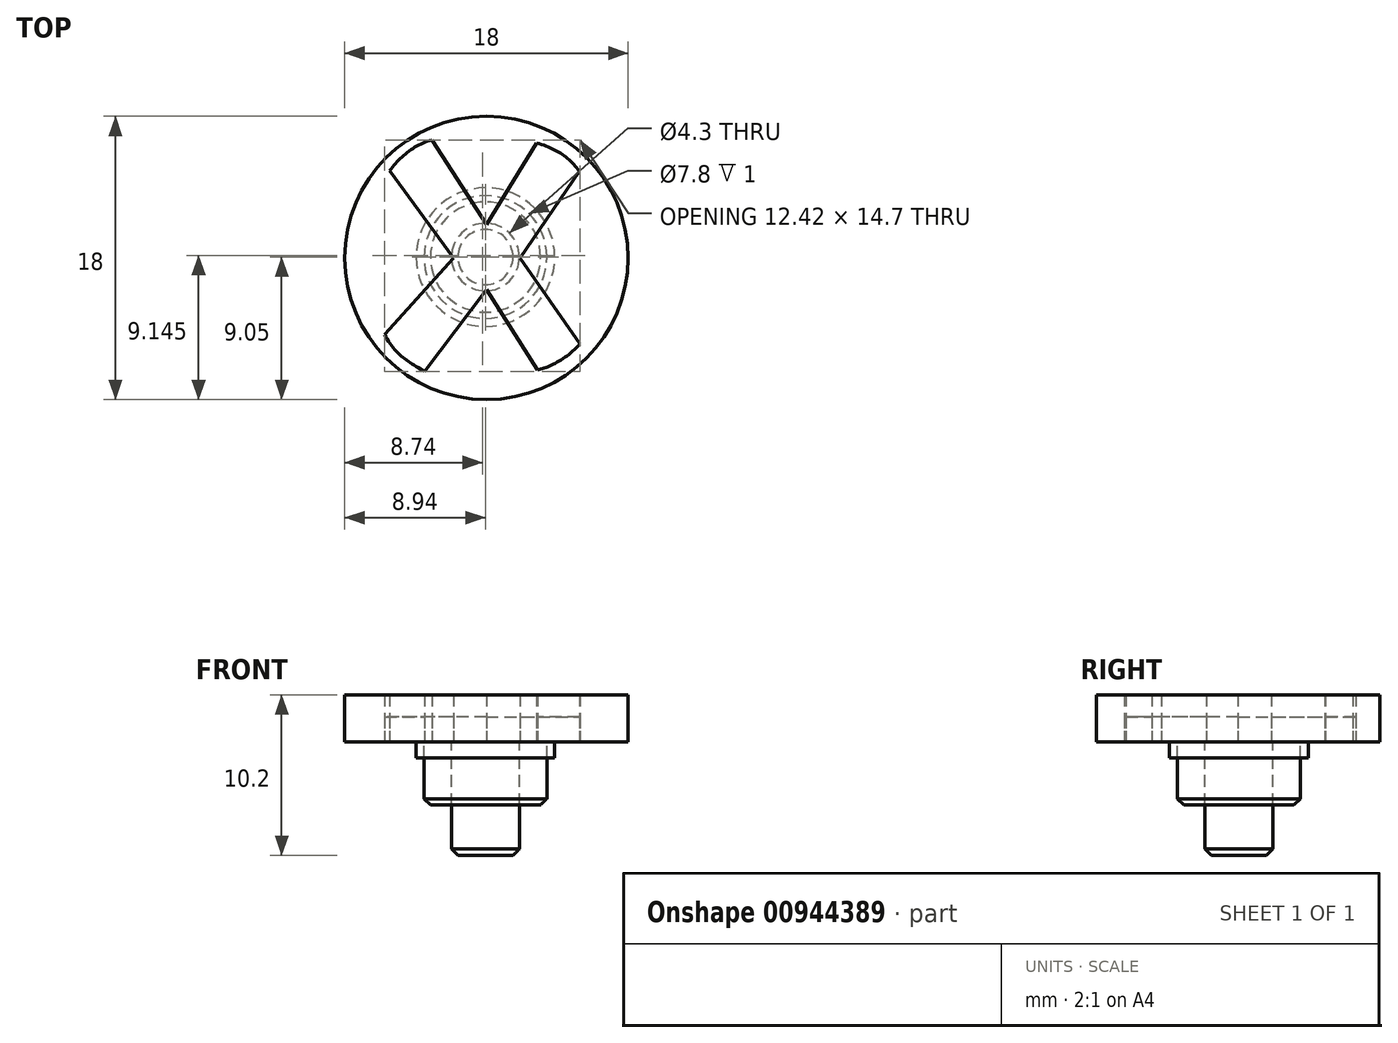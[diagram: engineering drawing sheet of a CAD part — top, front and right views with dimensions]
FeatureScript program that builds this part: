
annotation { "Feature Type Name" : "Feature", "Feature Type Description" : "" }
export const myFeature = defineFeature(function(context is Context, id is Id, definition is map)
    precondition{}
    {
        {
            var Q0;
            Q0=qCreatedBy(makeId("Top.planeOp"),FACE);
            var sketch = newSketch(context, id + "F0", { "sketchPlane" : qUnion([Q0])});
            skCircle(sketch, "E0", {"center": v(0, 0) * mm, "radius": 2.15 * mm});
            skCircle(sketch, "E1", {"center": v(0, 0) * mm, "radius": 3.9 * mm});
            skCircle(sketch, "E2", {"center": v(0, 0) * mm, "radius": 4.4 * mm});
            skCircle(sketch, "E3", {"center": v(0, 0) * mm, "radius": 9 * mm});
            skSolve(sketch);
        }
        {
            var Q0;
            Q0=makeQuery(id+"F0.imprint","IMPRINT",FACE,{"disambiguationData":[TD([[makeQuery(id+"F0.imprint","IMPRINT",EDGE,{"derivedFrom":sQuery(id+"F0.wireOp",EDGE,"E1")}),-1.0]])]});
            extrude(context, id + "F1", {"entities" : qUnion([Q0]), "depth" : -1 * mm, "offsetDistance" : 25 * mm});
        }
        {
            var Q0;
            Q0=makeQuery(id+"F0.imprint","IMPRINT",FACE,{"disambiguationData":[TD([[makeQuery(id+"F0.imprint","IMPRINT",EDGE,{"derivedFrom":sQuery(id+"F0.wireOp",EDGE,"E0")}),-1.0]])]});
            extrude(context, id + "F2", {"entities" : qUnion([Q0]), "depth" : -4 * mm, "offsetDistance" : 25 * mm});
        }
        {
            var Q0;
            Q0=makeQuery(id+"F0.imprint","IMPRINT",FACE,{"disambiguationData":[TD([[makeQuery(id+"F0.imprint","IMPRINT",EDGE,{"derivedFrom":sQuery(id+"F0.wireOp",EDGE,"E0")}),1.0]])]});
            extrude(context, id + "F3", {"entities" : qUnion([Q0]), "depth" : -7.2 * mm, "offsetDistance" : 25 * mm});
        }
        {
            var Q0;
            Q0=makeQuery(id+"F3.opExtrude","CAP_EDGE",EDGE,{"disambiguationData":[OSD([sQuery(id+"F0.wireOp",EDGE,"E0")])],"isStart":false});
            var Q1;
            Q1=makeQuery(id+"F2.opExtrude","CAP_EDGE",EDGE,{"disambiguationData":[OSD([sQuery(id+"F0.wireOp",EDGE,"E1")])],"isStart":false});
            chamfer(context, id + "F4", {"entities" : qUnion([Q0, Q1]), "width" : 0.4 * mm, "tangentPropagation" : true});
        }
        {
            var Q0;
            Q0=qCreatedBy(makeId("Top.planeOp"),FACE);
            var sketch = newSketch(context, id + "F5", { "sketchPlane" : qUnion([Q0])});
            skCircle(sketch, "E4", {"center": v(0.06, -0.05) * mm, "radius": 9 * mm});
            skLineSegment(sketch, "E5", {"start": v(0.06, -9.05) * mm, "end": v(0.06, 8.95) * mm, "construction": true});
            skLineSegment(sketch, "E6", {"start": v(-8.94, -0.05) * mm, "end": v(9.06, -0.05) * mm, "construction": true});
            skLineSegment(sketch, "E7", {"start": v(0.06, 2.06) * mm, "end": v(-3.8, 8.08) * mm});
            skLineSegment(sketch, "E8", {"start": v(0.06, 2.06) * mm, "end": v(3.78, 8.14) * mm});
            skLineSegment(sketch, "E9", {"start": v(0.06, -2.08) * mm, "end": v(-4.35, -7.9) * mm});
            skLineSegment(sketch, "E10", {"start": v(0.06, -2.08) * mm, "end": v(3.93, -8.18) * mm});
            skLineSegment(sketch, "E11", {"start": v(-2.04, -0.05) * mm, "end": v(-6.52, 6.08) * mm});
            skLineSegment(sketch, "E12", {"start": v(-2.04, -0.05) * mm, "end": v(-7.03, -5.6) * mm});
            skLineSegment(sketch, "E13", {"start": v(2.2, -0.05) * mm, "end": v(6.5, 6.23) * mm});
            skLineSegment(sketch, "E14", {"start": v(2.2, -0.05) * mm, "end": v(6.55, -6.29) * mm});
            skFitSpline(sketch, "E15", {"points": [v(-3.39, 7.44) * mm, v(-6.09, 5.49) * mm], "startDerivative": vector(-3.47, -0.92) * mm, "endDerivative": vector(-2.08, -2.73) * mm});
            skFitSpline(sketch, "E16", {"points": [v(-6.4, -4.9) * mm, v(-3.86, -7.25) * mm], "startDerivative": vector(1.88, -3.7) * mm, "endDerivative": vector(3.22, -1.82) * mm});
            skFitSpline(sketch, "E17", {"points": [v(3.3, -7.17) * mm, v(6, -5.51) * mm], "startDerivative": vector(2.31, 0.43) * mm, "endDerivative": vector(2.57, 2.85) * mm});
            skFitSpline(sketch, "E18", {"points": [v(5.98, 5.46) * mm, v(3.23, 7.25) * mm], "startDerivative": vector(-2.05, 2.67) * mm, "endDerivative": vector(-3.82, 1.07) * mm});
            skSolve(sketch);
        }
        {
            var Q0;
            {var subQ0=sQuery(id+"F5.wireOp",EDGE,"E11");var subQ1=sQuery(id+"F5.wireOp",EDGE,"E4");var subQ2=makeQuery(id+"F5.imprint","INTERSECT",VERTEX,{"derivedFrom":[subQ1,subQ0]});Q0=makeQuery(id+"F5.imprint","IMPRINT",FACE,{"disambiguationData":[TD([[makeQuery(id+"F5.imprint","IMPRINT",EDGE,{"disambiguationData":[TD([[subQ2,-1.0]])],"derivedFrom":subQ1}),1.0]])]});}
            var Q1;
            {var subQ1=sQuery(id+"F5.wireOp",EDGE,"E7");var subQ4=sQuery(id+"F5.wireOp",EDGE,"E4");var subQ5=makeQuery(id+"F5.imprint","INTERSECT",VERTEX,{"derivedFrom":[subQ4,subQ1]});Q1=makeQuery(id+"F5.imprint","IMPRINT",FACE,{"disambiguationData":[TD([[makeQuery(id+"F5.imprint","IMPRINT",EDGE,{"disambiguationData":[TD([[subQ5,1.0]])],"derivedFrom":subQ4}),1.0]])]});}
            var Q2;
            {var subQ0=sQuery(id+"F5.wireOp",EDGE,"E13");var subQ1=sQuery(id+"F5.wireOp",EDGE,"E4");var subQ2=makeQuery(id+"F5.imprint","INTERSECT",VERTEX,{"derivedFrom":[subQ1,subQ0]});Q2=makeQuery(id+"F5.imprint","IMPRINT",FACE,{"disambiguationData":[TD([[makeQuery(id+"F5.imprint","IMPRINT",EDGE,{"disambiguationData":[TD([[subQ2,1.0]])],"derivedFrom":subQ1}),1.0]])]});}
            var Q3;
            {var subQ1=sQuery(id+"F5.wireOp",EDGE,"E9");var subQ4=sQuery(id+"F5.wireOp",EDGE,"E4");var subQ5=makeQuery(id+"F5.imprint","INTERSECT",VERTEX,{"derivedFrom":[subQ4,subQ1]});Q3=makeQuery(id+"F5.imprint","IMPRINT",FACE,{"disambiguationData":[TD([[makeQuery(id+"F5.imprint","IMPRINT",EDGE,{"disambiguationData":[TD([[subQ5,-1.0]])],"derivedFrom":subQ4}),1.0]])]});}
            var Q4;
            {var subQ5=sQuery(id+"F5.wireOp",EDGE,"E18");Q4=makeQuery(id+"F5.imprint","IMPRINT",FACE,{"disambiguationData":[TD([[makeQuery(id+"F5.imprint","IMPRINT",EDGE,{"derivedFrom":subQ5}),-1.0]])]});}
            var Q5;
            {var subQ5=sQuery(id+"F5.wireOp",EDGE,"E15");Q5=makeQuery(id+"F5.imprint","IMPRINT",FACE,{"disambiguationData":[TD([[makeQuery(id+"F5.imprint","IMPRINT",EDGE,{"derivedFrom":subQ5}),-1.0]])]});}
            var Q6;
            {var subQ5=sQuery(id+"F5.wireOp",EDGE,"E17");Q6=makeQuery(id+"F5.imprint","IMPRINT",FACE,{"disambiguationData":[TD([[makeQuery(id+"F5.imprint","IMPRINT",EDGE,{"derivedFrom":subQ5}),-1.0]])]});}
            var Q7;
            {var subQ5=sQuery(id+"F5.wireOp",EDGE,"E16");Q7=makeQuery(id+"F5.imprint","IMPRINT",FACE,{"disambiguationData":[TD([[makeQuery(id+"F5.imprint","IMPRINT",EDGE,{"derivedFrom":subQ5}),-1.0]])]});}
            extrude(context, id + "F6", {"entities" : qUnion([Q0, Q1, Q2, Q3, Q4, Q5, Q6, Q7]), "depth" : 3 * mm, "offsetDistance" : 25 * mm});
        }
        {
            var Q0;
            {var subQ0=sQuery(id+"F5.wireOp",EDGE,"E15");Q0=makeQuery(id+"F5.imprint","IMPRINT",FACE,{"disambiguationData":[TD([[makeQuery(id+"F5.imprint","IMPRINT",EDGE,{"derivedFrom":subQ0}),1.0]])]});}
            extrude(context, id + "F7", {"entities" : qUnion([Q0]), "depth" : 1.6 * mm, "offsetDistance" : 25 * mm});
        }
    });
